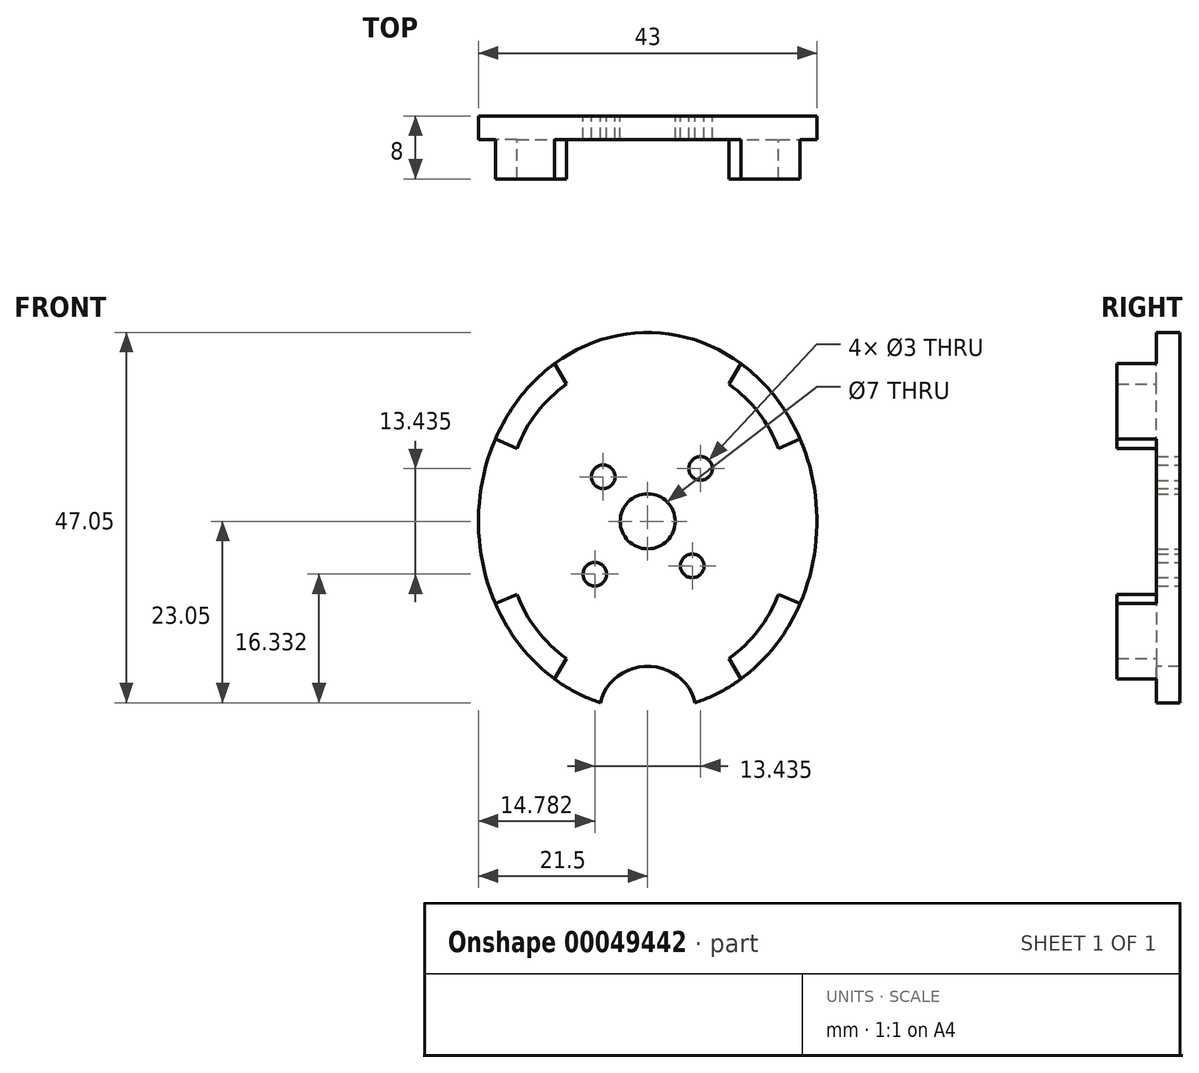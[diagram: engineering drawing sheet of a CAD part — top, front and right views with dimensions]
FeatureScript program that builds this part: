
annotation { "Feature Type Name" : "Feature", "Feature Type Description" : "" }
export const myFeature = defineFeature(function(context is Context, id is Id, definition is map)
    precondition{}
    {
        {
            var Q0;
            Q0=qCreatedBy(makeId("Front.planeOp"),FACE);
            var sketch = newSketch(context, id + "F0", { "sketchPlane" : qUnion([Q0])});
            skEllipticalArc(sketch, "E0", {});
            skCircle(sketch, "E1", {"center": v(0, 0) * mm, "radius": 8 * mm, "construction": true});
            skLineSegment(sketch, "E2", {"start": v(0, 0) * mm, "end": v(5.66, 5.66) * mm, "construction": true});
            skCircle(sketch, "E3.1.0", {"center": v(5.66, -5.66) * mm, "radius": 1.5 * mm});
            skCircle(sketch, "E3.3.0", {"center": v(-5.66, 5.66) * mm, "radius": 1.5 * mm});
            skLineSegment(sketch, "E3.anchor2", {"start": v(0, 0) * mm, "end": v(-5.66, 5.66) * mm, "construction": true});
            skEllipticalArc(sketch, "E4", {});
            skPoint(sketch, "E5.orphan", {"position": v(0, -18.62) * mm});
            skCircle(sketch, "E6", {"center": v(0, 0) * mm, "radius": 3.5 * mm});
            skCircle(sketch, "E7", {"center": v(0, 0) * mm, "radius": 9.5 * mm, "construction": true});
            skLineSegment(sketch, "E8", {"start": v(0, 0) * mm, "end": v(-6.72, -6.72) * mm, "construction": true});
            skCircle(sketch, "E9", {"center": v(-6.72, -6.72) * mm, "radius": 1.5 * mm});
            skCircle(sketch, "E10.MirrorC", {"center": v(6.72, 6.72) * mm, "radius": 1.5 * mm});
            const initialGuessF0  = {"E0": [0, 0, 0, 1, 0.024, 0.0215, 3.4231890954044655, 2.859996211775119], "E4": [0, -0.024, -1, 0, 0.00606221443115755, 0.005581033474772104, 3.3117880856813957, 6.112989875087983]};
            skSetInitialGuess(sketch, initialGuessF0);
            skSolve(sketch);
        }
        {
            var Q0;
            Q0=makeQuery(id+"F0.imprint","IMPRINT",FACE,{"disambiguationData":[TD([[makeQuery(id+"F0.imprint","IMPRINT",EDGE,{"derivedFrom":sQuery(id+"F0.wireOp",EDGE,"E0")}),1.0]])]});
            extrude(context, id + "F1", {"entities" : qUnion([Q0]), "depth" : 3 * mm});
        }
        {
            var Q0;
            Q0=makeQuery(id+"F1.opExtrude","CAP_FACE",FACE,{"disambiguationData":[OSD([sQuery(id+"F0.wireOp",EDGE,"E0"),sQuery(id+"F0.wireOp",EDGE,"ee09b118-8e07-4cee-be3b-c7187508dda0"),sQuery(id+"F0.wireOp",EDGE,"E3.1.0"),sQuery(id+"F0.wireOp",EDGE,"E3.2.0"),sQuery(id+"F0.wireOp",EDGE,"E3.3.0"),sQuery(id+"F0.wireOp",EDGE,"E4")])],"isStart":false});
            var sketch = newSketch(context, id + "F2", { "sketchPlane" : qUnion([Q0])});
            skLineSegment(sketch, "E11", {"start": v(0, 0) * mm, "end": v(16.01, 16.01) * mm, "construction": true});
            skEllipticalArc(sketch, "E12", {});
            skLineSegment(sketch, "E13", {"start": v(16.6, 9.28) * mm, "end": v(19.36, 10.45) * mm});
            skLineSegment(sketch, "E14", {"start": v(10.33, 17.41) * mm, "end": v(11.83, 20.04) * mm});
            skLineSegment(sketch, "E15.MirrorCS", {"start": v(10.33, -17.41) * mm, "end": v(11.83, -20.04) * mm});
            skEllipticalArc(sketch, "E16.MirrorCS", {});
            skLineSegment(sketch, "E17.MirrorCS", {"start": v(16.6, -9.28) * mm, "end": v(19.36, -10.45) * mm});
            skLineSegment(sketch, "E18.MirrorCS", {"start": v(-10.33, 17.41) * mm, "end": v(-11.83, 20.04) * mm});
            skEllipticalArc(sketch, "E19.MirrorCS", {});
            skLineSegment(sketch, "E20.MirrorCS", {"start": v(-16.6, 9.28) * mm, "end": v(-19.36, 10.45) * mm});
            skArc(sketch, "E21", {"start": v(16.6, 9.28) * mm, "mid": v(14.07, 13.81) * mm, "end": v(10.33, 17.41) * mm});
            skArc(sketch, "E22.MirrorCS", {"start": v(-16.6, 9.28) * mm, "mid": v(-14.07, 13.81) * mm, "end": v(-10.33, 17.41) * mm});
            skArc(sketch, "E23.MirrorCS", {"start": v(16.6, -9.28) * mm, "mid": v(14.07, -13.81) * mm, "end": v(10.33, -17.41) * mm});
            skLineSegment(sketch, "E24.MirrorCS", {"start": v(-16.6, -9.28) * mm, "end": v(-19.36, -10.45) * mm});
            skEllipticalArc(sketch, "E25.MirrorCS", {});
            skArc(sketch, "E26.MirrorCS", {"start": v(-16.6, -9.28) * mm, "mid": v(-14.07, -13.81) * mm, "end": v(-10.33, -17.41) * mm});
            skLineSegment(sketch, "E27.MirrorCS", {"start": v(-10.33, -17.41) * mm, "end": v(-11.83, -20.04) * mm});
            const initialGuessF2  = {"E12": [0, 0, 1, 0, 0.0215, 0.024, 0.45031396467637297, 0.9883681275279574], "E16.MirrorCS": [0, 0, 1, 0, 0.0215, 0.024, 5.294817179651629, 5.832871342503212], "E19.MirrorCS": [0, 0, -1, 0, 0.0215, 0.024, 5.294817179651629, 5.832871342503213], "E25.MirrorCS": [0, 0, -1, 0, 0.0215, 0.024, 0.45031396467637386, 0.9883681275279574]};
            skSetInitialGuess(sketch, initialGuessF2);
            skSolve(sketch);
        }
        {
            var Q0;
            Q0=qSketchRegion(id+"F2",true);
            extrude(context, id + "F3", {"entities" : qUnion([Q0]), "operationType" : NewBodyOperationType.ADD, "depth" : 5 * mm});
        }
    });
